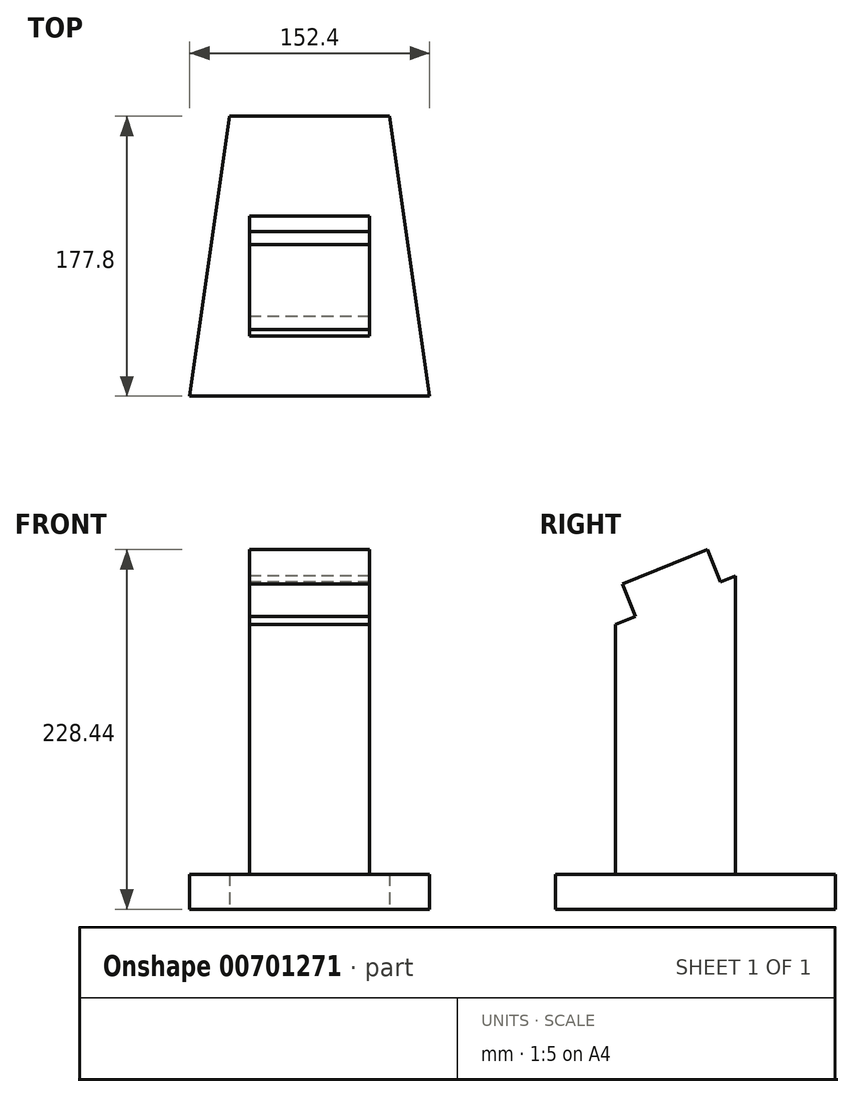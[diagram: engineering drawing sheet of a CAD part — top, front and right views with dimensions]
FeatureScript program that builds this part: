
annotation { "Feature Type Name" : "Feature", "Feature Type Description" : "" }
export const myFeature = defineFeature(function(context is Context, id is Id, definition is map)
    precondition{}
    {
        {
            var Q0;
            Q0=qCreatedBy(makeId("Top.planeOp"),FACE);
            var sketch = newSketch(context, id + "F0", { "sketchPlane" : qUnion([Q0])});
            skLineSegment(sketch, "E0.top", {"start": v(-76.2, -63.5) * mm, "end": v(76.2, -63.5) * mm});
            skPoint(sketch, "E0.middle", {"position": v(0, 0) * mm});
            skLineSegment(sketch, "E1", {"start": v(-76.2, -63.5) * mm, "end": v(-50.8, 114.3) * mm});
            skLineSegment(sketch, "E2", {"start": v(-50.8, 114.3) * mm, "end": v(50.8, 114.3) * mm});
            skLineSegment(sketch, "E3", {"start": v(50.8, 114.3) * mm, "end": v(76.2, -63.5) * mm});
            skPoint(sketch, "E0.left.start.orphan", {"position": v(-76.2, 63.5) * mm});
            skPoint(sketch, "E0.right.start.orphan", {"position": v(76.2, 63.5) * mm});
            skSolve(sketch);
        }
        {
            var Q0;
            Q0 = qSketchRegion(id + "F0", true);
            extrude(context, id + "F1", {"entities" : qUnion([Q0]), "depth" : 22.22 * mm, "offsetDistance" : 25.4 * mm});
        }
        {
            var Q0;
            Q0=qCreatedBy(makeId("Right.planeOp"),FACE);
            var sketch = newSketch(context, id + "F2", { "sketchPlane" : qUnion([Q0])});
            skLineSegment(sketch, "E4", {"start": v(-25.4, 22.23) * mm, "end": v(-25.4, 180.97) * mm});
            skLineSegment(sketch, "E5", {"start": v(-25.4, 180.97) * mm, "end": v(50.8, 211.76) * mm});
            skLineSegment(sketch, "E6", {"start": v(50.8, 211.76) * mm, "end": v(50.8, 22.23) * mm});
            skLineSegment(sketch, "E7.0", {"start": v(114.3, 22.23) * mm, "end": v(-63.5, 22.23) * mm});
            skLineSegment(sketch, "E8", {"start": v(-12.92, 186.02) * mm, "end": v(-21.24, 206.63) * mm});
            skLineSegment(sketch, "E9", {"start": v(-21.24, 206.63) * mm, "end": v(32.75, 228.44) * mm});
            skLineSegment(sketch, "E10", {"start": v(32.75, 228.44) * mm, "end": v(41.07, 207.83) * mm});
            skSolve(sketch);
        }
        {
            var Q0;
            Q0 = qSketchRegion(id + "F2", true);
            extrude(context, id + "F3", {"entities" : qUnion([Q0]), "endBound" : BoundingType.SYMMETRIC, "depth" : 76.2 * mm, "offsetDistance" : 25.4 * mm});
        }
    });
